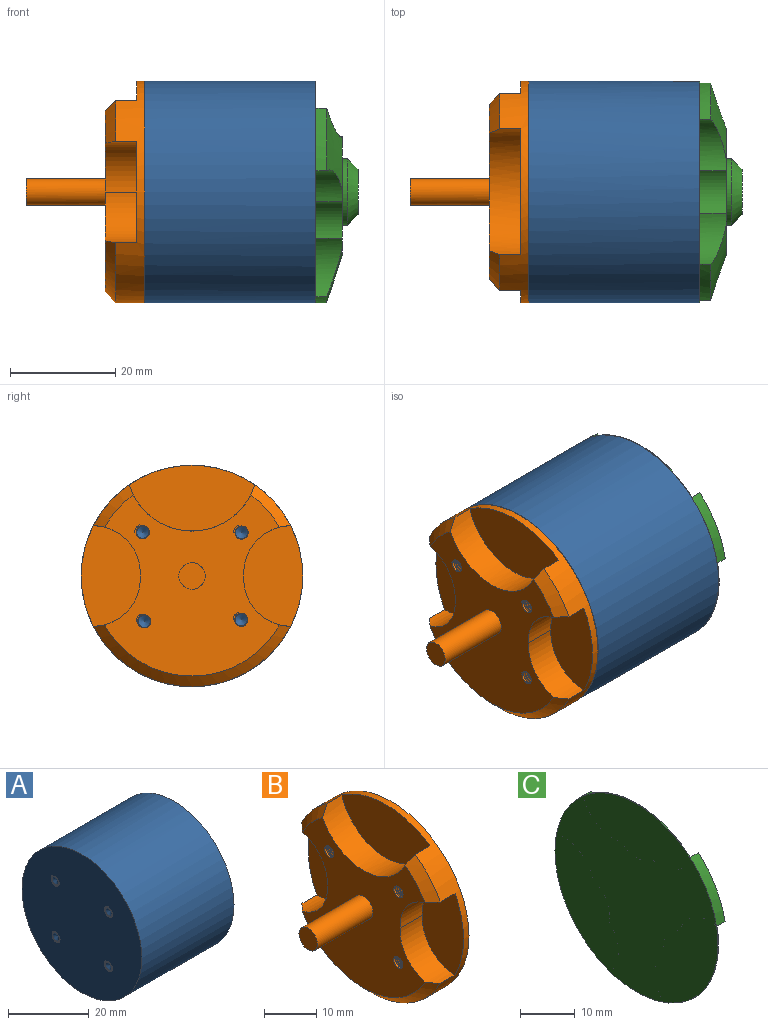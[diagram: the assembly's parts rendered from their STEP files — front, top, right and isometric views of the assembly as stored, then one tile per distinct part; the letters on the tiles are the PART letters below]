
ASSEMBLY  parts=3 mates=1
PART A: 27 faces, bbox 32.6x42.1x42.1 mm
  f0: plane 0.38x0.27mm, normal (0,0,-1), area 0.1mm2, adj f6,f7,f8,f9
  f1: plane 0.38x0.27mm, normal (0,0,-1), area 0.1mm2, adj f10,f11,f12,f13
  f2: plane 0.38x0.27mm, normal (0,0,-1), area 0.1mm2, adj f14,f15,f16,f17
  f3: plane 0.38x0.27mm, normal (0,0,-1), area 0.1mm2, adj f18,f19,f20,f21
  f4: cone r=1.25mm half-angle=59deg, axis (-1,0,0), area 4.9mm2, adj f24
  f5: cone r=1.25mm half-angle=59deg, axis (-1,0,0), area 4.9mm2, adj f24
  f6: bspline ~3.51x3.04mm, area 14.9mm2, adj f0,f7,f9,f24
  f7: cylinder r=1.25mm len=2.82mm, axis (-1,0,0), area 15.5mm2, adj f0,f6,f8,f24
  f8: bspline ~3.51x3.04mm, area 13.7mm2, adj f0,f7,f9,f24
  f9: cylinder r=1.52mm len=3.04mm, axis (1,0,0), area 2.9mm2, adj f0,f6,f8,f24
  f10: bspline ~3.51x3.04mm, area 14.9mm2, adj f1,f11,f13,f24
  f11: cylinder r=1.25mm len=2.82mm, axis (-1,0,0), area 15.5mm2, adj f1,f10,f12,f24
  f12: bspline ~3.51x3.04mm, area 13.7mm2, adj f1,f11,f13,f24
  f13: cylinder r=1.52mm len=3.04mm, axis (1,0,0), area 2.9mm2, adj f1,f10,f12,f24
  f14: bspline ~3.51x3.04mm, area 14.9mm2, adj f2,f15,f17,f24
  f15: cylinder r=1.25mm len=2.82mm, axis (-1,0,0), area 15.5mm2, adj f2,f14,f16,f24
  f16: bspline ~3.51x3.04mm, area 13.7mm2, adj f2,f15,f17,f24
  f17: cylinder r=1.52mm len=3.04mm, axis (1,0,0), area 2.9mm2, adj f2,f14,f16,f24
  f18: bspline ~3.51x3.04mm, area 14.9mm2, adj f3,f19,f21,f24
  f19: cylinder r=1.25mm len=2.82mm, axis (-1,0,0), area 15.5mm2, adj f3,f18,f20,f24
  f20: bspline ~3.51x3.04mm, area 13.7mm2, adj f3,f19,f21,f24
  f21: cylinder r=1.52mm len=3.04mm, axis (1,0,0), area 2.9mm2, adj f3,f18,f20,f24
  f22: cone r=1.25mm half-angle=59deg, axis (-1,0,0), area 4.9mm2, adj f24
  f23: cone r=1.25mm half-angle=59deg, axis (-1,0,0), area 4.9mm2, adj f24
  f24: plane 42.14x42.14mm, normal (-1,0,0), area 1364.6mm2, adj f4,f5,f6,f7,f8,f9,f10,f11
  f25: cylinder r=21mm len=42mm, axis (-1,0,0), area 4260.6mm2, adj f24,f26
  f26: plane 42x42mm, normal (1,0,0), area 1385.4mm2, adj f25
PART B: 36 faces, bbox 22.8x42.1x42.1 mm
  f0: plane 5x5mm, normal (-1,0,0), area 19.6mm2, adj f1
  f1: cylinder r=2.5mm len=15mm, axis (1,0,0), area 235.6mm2, adj f0,f29
  f2: cone r=21mm half-angle=45deg, axis (1,0,0), area 26.3mm2, adj f3,f12,f13,f29
  f3: cylinder r=8.95mm len=9.54mm, axis (-1,0,0), area 85.4mm2, adj f2,f4,f5,f13,f29
  f4: plane 19.07x11.18mm, normal (-1,0,0), area 164.6mm2, adj f3,f5,f13
  f5: cylinder r=8.95mm len=9.54mm, axis (-1,0,0), area 85.4mm2, adj f3,f4,f6,f13,f29
  f6: cone r=21mm half-angle=45deg, axis (1,0,0), area 122.3mm2, adj f5,f7,f13,f29
  f7: cylinder r=8.95mm len=9.54mm, axis (-1,0,0), area 85.4mm2, adj f6,f8,f9,f13,f29
  f8: plane 19.07x11.18mm, normal (-1,0,0), area 164.6mm2, adj f7,f9,f13
  f9: cylinder r=8.95mm len=9.54mm, axis (-1,0,0), area 85.4mm2, adj f7,f8,f10,f13,f29
  f10: cone r=21mm half-angle=45deg, axis (1,0,0), area 26.3mm2, adj f9,f12,f13,f29
  f11: plane 23.84x12.49mm, normal (-1,0,0), area 213.7mm2, adj f12,f13
  f12: cylinder r=12.49mm len=23.84mm, axis (-1,0,0), area 186mm2, adj f2,f10,f11,f13,f29
  f13: cylinder r=21mm len=42mm, axis (-1,0,0), area 463.8mm2, adj f2,f3,f4,f5,f6,f7,f8,f9
  f14: plane 0.38x0.27mm, normal (0,0,1), area 0.1mm2, adj f15,f16,f17,f18
  f15: bspline ~7.49x3.51mm, area 39.2mm2, adj f14,f17,f18,f35
  f16: bspline ~7.66x3.51mm, area 40.5mm2, adj f14,f17,f18,f35
  f17: cylinder r=1.52mm len=7.33mm, axis (1,0,0), area 17.5mm2, adj f14,f15,f16,f35
  f18: cylinder r=1.25mm len=7.48mm, axis (-1,0,0), area 13.4mm2, adj f14,f15,f16,f29,f35
  f19: plane 0.38x0.27mm, normal (0,0,1), area 0.1mm2, adj f20,f21,f22,f23
  f20: bspline ~7.49x3.51mm, area 39.2mm2, adj f19,f22,f23,f35
  f21: bspline ~7.66x3.51mm, area 40.5mm2, adj f19,f22,f23,f35
  f22: cylinder r=1.52mm len=7.33mm, axis (1,0,0), area 17.5mm2, adj f19,f20,f21,f35
  f23: cylinder r=1.25mm len=7.48mm, axis (-1,0,0), area 13.4mm2, adj f19,f20,f21,f29,f35
  f24: plane 0.38x0.27mm, normal (0,0,1), area 0.1mm2, adj f25,f26,f27,f28
  f25: bspline ~7.49x3.51mm, area 39.2mm2, adj f24,f27,f28,f35
  f26: bspline ~7.66x3.51mm, area 40.5mm2, adj f24,f27,f28,f35
  f27: cylinder r=1.52mm len=7.33mm, axis (1,0,0), area 17.5mm2, adj f24,f25,f26,f35
  f28: cylinder r=1.25mm len=7.48mm, axis (-1,0,0), area 13.4mm2, adj f24,f25,f26,f29,f35
  f29: plane 34.38x33.18mm, normal (-1,0,0), area 680mm2, adj f1,f2,f3,f5,f6,f7,f9,f10
  f30: plane 0.38x0.27mm, normal (0,0,1), area 0.1mm2, adj f31,f32,f33,f34
  f31: bspline ~7.49x3.51mm, area 39.2mm2, adj f30,f33,f34,f35
  f32: bspline ~7.66x3.51mm, area 40.5mm2, adj f30,f33,f34,f35
  f33: cylinder r=1.52mm len=7.33mm, axis (1,0,0), area 17.5mm2, adj f30,f31,f32,f35
  f34: cylinder r=1.25mm len=7.48mm, axis (-1,0,0), area 13.4mm2, adj f29,f30,f31,f32,f35
  f35: plane 42.14x42.14mm, normal (1,0,0), area 1361.8mm2, adj f13,f15,f16,f17,f18,f20,f21,f22
PART C: 21 faces, bbox 8.1x42x42 mm
  f0: cylinder r=21mm len=42mm, axis (-1,0,0), area 102.3mm2, adj f5,f6,f8,f10,f11,f12,f13,f14
  f1: plane 23.99x22.56mm, normal (1,0,0), area 263.3mm2, adj f2,f5,f6,f7,f9,f10,f11,f13
  f2: cylinder r=6.33mm len=12.66mm, axis (1,0,0), area 39.8mm2, adj f1,f4
  f3: plane 8.66x8.66mm, normal (1,0,0), area 58.9mm2, adj f4
  f4: cone r=4.33mm half-angle=45deg, axis (-1,0,0), area 94.7mm2, adj f2,f3
  f5: cylinder r=7.85mm len=11.09mm, axis (1,0,0), area 47.7mm2, adj f0,f1,f7,f8,f19
  f6: cylinder r=7.85mm len=9.47mm, axis (1,0,0), area 47.7mm2, adj f0,f1,f7,f8,f18
  f7: cylinder r=5.68mm len=6.95mm, axis (1,0,0), area 44.6mm2, adj f1,f5,f6,f8
  f8: plane 24.05x16.3mm, normal (1,0,0), area 235.4mm2, adj f0,f5,f6,f7
  f9: cylinder r=5.68mm len=6.95mm, axis (1,0,0), area 44.6mm2, adj f1,f10,f11,f12
  f10: cylinder r=7.85mm len=9.47mm, axis (1,0,0), area 47.7mm2, adj f0,f1,f9,f12,f17
  f11: cylinder r=7.85mm len=11.09mm, axis (1,0,0), area 47.7mm2, adj f0,f1,f9,f12,f19
  f12: plane 24.05x16.3mm, normal (1,0,0), area 235.4mm2, adj f0,f9,f10,f11
  f13: cylinder r=7.85mm len=9.75mm, axis (1,0,0), area 47.7mm2, adj f0,f1,f15,f16,f18
  f14: cylinder r=7.85mm len=9.75mm, axis (1,0,0), area 47.7mm2, adj f0,f1,f15,f16,f17
  f15: cylinder r=5.68mm len=8.03mm, axis (1,0,0), area 44.6mm2, adj f1,f13,f14,f16
  f16: plane 27.52x12.1mm, normal (1,0,0), area 235.4mm2, adj f0,f13,f14,f15
  f17: cone r=12mm half-angle=71.9deg, axis (-1,0,0), area 101.7mm2, adj f0,f1,f10,f14
  f18: cone r=12mm half-angle=71.9deg, axis (-1,0,0), area 101.7mm2, adj f0,f1,f6,f13
  f19: cone r=12mm half-angle=71.9deg, axis (-1,0,0), area 101.7mm2, adj f0,f1,f5,f11
  f20: plane 42x42mm, normal (-1,0,0), area 1385.4mm2, adj f0
PLACE A t=(-9.53,4.99,1.48)mm
PLACE B t=(-9.53,4.99,1.48)mm
PLACE C t=(-9.56,4.99,1.48)mm
MATE revolute A.f25 <-> C.f0  axis (1,0,0) through (30.32,4.99,1.48)mm
